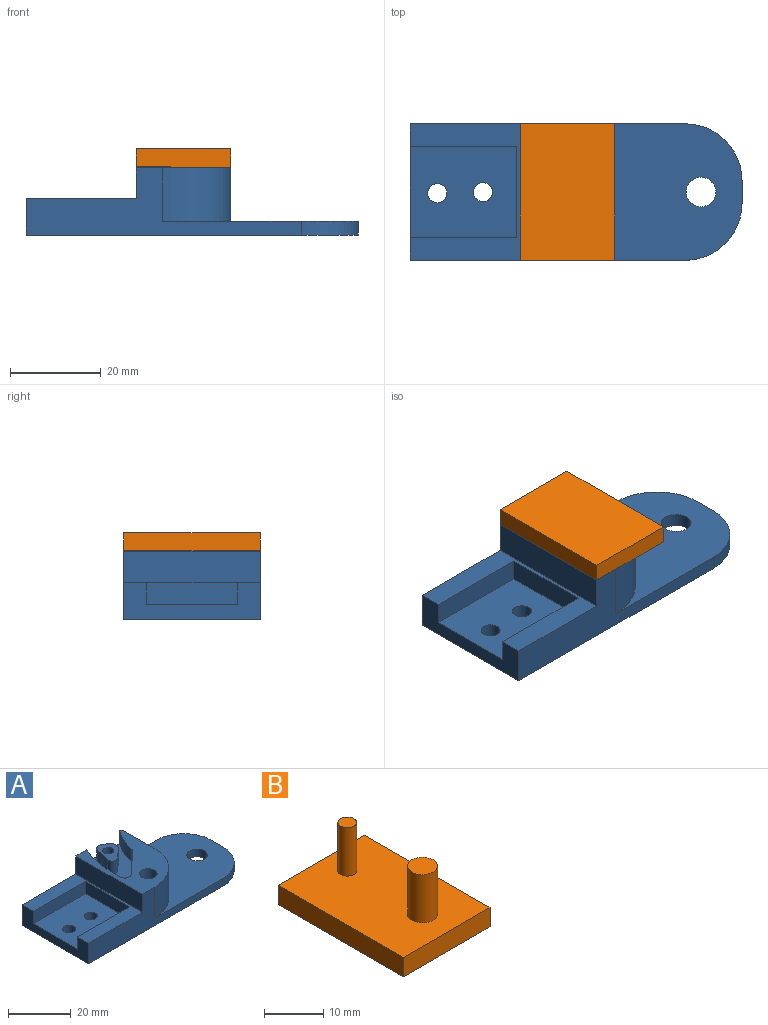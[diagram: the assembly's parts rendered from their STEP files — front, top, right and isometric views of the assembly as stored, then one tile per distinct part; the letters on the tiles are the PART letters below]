
ASSEMBLY  parts=2 mates=1
PART A: 37 faces, bbox 73x30x15 mm
  f0: cylinder r=2.5mm len=5mm, axis (0,0,-1), area 23.6mm2, adj f28,f29,f32,f34
  f1: cylinder r=2mm len=5mm, axis (0,0,-1), area 6.2mm2, adj f3,f4,f16,f28
  f2: cylinder r=2mm len=5mm, axis (0,0,-1), area 22.3mm2, adj f3,f4,f21,f28
  f3: plane 9.42x8.78mm, normal (-0.68,0.73,0), area 64.4mm2, adj f1,f2,f4,f28
  f4: plane 30x20.75mm, normal (0,0,1), area 326.2mm2, adj f1,f2,f3,f5,f6,f14,f15,f16
  f5: plane 14x12mm, normal (1,0,0), area 168mm2, adj f4,f6,f14,f18
  f6: cylinder r=15mm len=15mm, axis (0,0,1), area 282.7mm2, adj f4,f5,f18,f25
  f7: cylinder r=2.1mm len=4.2mm, axis (0,0,-1), area 42.2mm2, adj f12,f27
  f8: cylinder r=2.1mm len=4.2mm, axis (0,0,-1), area 42.2mm2, adj f12,f27
  f9: plane 23.5x4.8mm, normal (0,1,0), area 112.8mm2, adj f10,f12,f13,f26
  f10: plane 20x4.8mm, normal (-1,0,0), area 96mm2, adj f9,f11,f12,f13
  f11: plane 23.5x4.8mm, normal (0,-1,0), area 112.8mm2, adj f10,f12,f13,f26
  f12: plane 23.5x20mm, normal (0,0,1), area 442.3mm2, adj f7,f8,f9,f10,f11,f26
  f13: plane 30x24.25mm, normal (0,0,1), area 257.5mm2, adj f9,f10,f11,f23,f24,f25,f26
  f14: cylinder r=1mm len=12mm, axis (0,0,1), area 17.6mm2, adj f4,f5,f15,f18,f24,f28
  f15: cylinder r=1mm len=5mm, axis (0,0,1), area 3.5mm2, adj f4,f14,f16,f28
  f16: cylinder r=25mm len=9.49mm, axis (0,0,-1), area 52.2mm2, adj f1,f4,f15,f28
  f17: cylinder r=12.5mm len=12.5mm, axis (0,0,1), area 58.9mm2, adj f18,f19,f25,f27
  f18: plane 43x30mm, normal (0,0,1), area 788.3mm2, adj f5,f6,f14,f17,f19,f20,f22,f24
  f19: plane 5x3mm, normal (1,0,0), area 15mm2, adj f17,f18,f20,f27
  f20: cylinder r=12.5mm len=12.5mm, axis (0,0,1), area 58.9mm2, adj f18,f19,f24,f27
  f21: cylinder r=38mm len=18.46mm, axis (0,0,-1), area 94.4mm2, adj f2,f4,f24,f28
  f22: cylinder r=3.25mm len=6.5mm, axis (0,0,-1), area 61.3mm2, adj f18,f27
  f23: plane 30x7mm, normal (-1,0,0), area 210mm2, adj f4,f13,f24,f25
  f24: plane 60.5x15mm, normal (0,1,0), area 465.1mm2, adj f4,f13,f14,f18,f20,f21,f23,f26
  f25: plane 60.5x15mm, normal (0,-1,0), area 371.7mm2, adj f4,f6,f13,f17,f18,f23,f26,f27
  f26: plane 30x8mm, normal (-1,0,0), area 144mm2, adj f9,f11,f12,f13,f24,f25,f27
  f27: plane 73x30mm, normal (0,0,-1), area 2027.9mm2, adj f7,f8,f17,f19,f20,f22,f24,f25
  f28: plane 20.28x18.26mm, normal (0,0,1), area 174.5mm2, adj f0,f1,f2,f3,f14,f15,f16,f21
  f29: plane 9.6x7.79mm, normal (0,0,1), area 39.2mm2, adj f0,f30,f31,f32,f33,f34,f35
  f30: cylinder r=34.6mm len=5mm, axis (0,0,-1), area 20.1mm2, adj f28,f29,f31,f33
  f31: cylinder r=1.75mm len=5mm, axis (0,0,-1), area 21.9mm2, adj f28,f29,f30,f32
  f32: plane 5x4.05mm, normal (0.68,-0.73,0), area 27.6mm2, adj f0,f28,f29,f31
  f33: extruded ~5.51x5mm, area 40.8mm2, adj f28,f29,f30,f34
  f34: plane 5x0mm, normal (0.41,-0.91,0), area 0mm2, adj f0,f28,f29,f33
  f35: cylinder r=1.75mm len=15mm, axis (0,0,1), area 164.6mm2, adj f27,f29
  f36: cylinder r=2.79mm len=15mm, axis (0,0,1), area 263.3mm2, adj f4,f27
PART B: 10 faces, bbox 20.8x30x14 mm
  f0: plane 30x4mm, normal (-1,0,0), area 120mm2, adj f1,f3,f4,f5
  f1: plane 20.75x4mm, normal (0,-1,0), area 83mm2, adj f0,f2,f4,f5
  f2: plane 30x4mm, normal (1,0,0), area 120mm2, adj f1,f3,f4,f5
  f3: plane 20.75x4mm, normal (0,1,0), area 83mm2, adj f0,f2,f4,f5
  f4: plane 30x20.75mm, normal (0,0,1), area 594.3mm2, adj f0,f1,f2,f3,f6,f8
  f5: plane 30x20.75mm, normal (0,0,-1), area 622.5mm2, adj f0,f1,f2,f3
  f6: cylinder r=1.59mm len=10mm, axis (0,0,-1), area 99.7mm2, adj f4,f7
  f7: plane 3.18x3.18mm, normal (0,0,1), area 7.9mm2, adj f6
  f8: cylinder r=2.54mm len=10mm, axis (0,0,-1), area 159.6mm2, adj f4,f9
  f9: plane 5.08x5.08mm, normal (0,0,1), area 20.3mm2, adj f8
PLACE A t=(-13.27,2.17,-3.68)mm
PLACE B rot(axis=(0,1,0),180deg) t=(31.73,2.17,15.25)mm
MATE cylindrical B.f8 <-> A.f36  axis (0,0,1) through (20.42,8.88,6.25)mm
